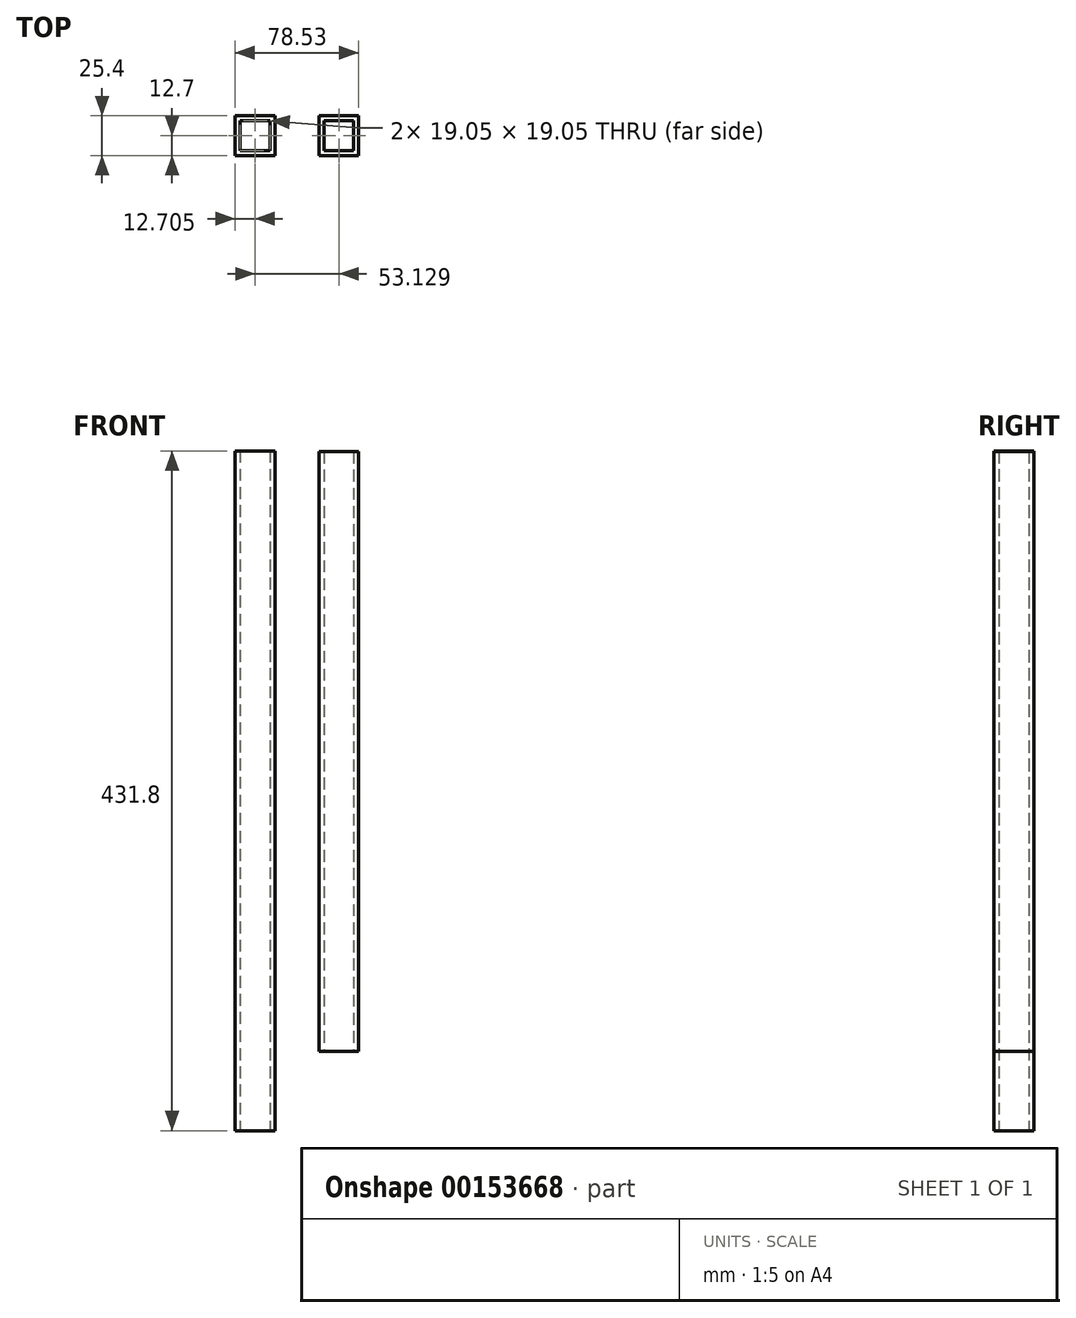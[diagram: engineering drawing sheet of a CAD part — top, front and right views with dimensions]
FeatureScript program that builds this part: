
annotation { "Feature Type Name" : "Feature", "Feature Type Description" : "" }
export const myFeature = defineFeature(function(context is Context, id is Id, definition is map)
    precondition{}
    {
        {
            var Q0;
            Q0=qCreatedBy(makeId("Front.planeOp"),FACE);
            var sketch = newSketch(context, id + "F0", { "sketchPlane" : qUnion([Q0])});
            skLineSegment(sketch, "E0.bottom", {"start": v(-31.27, 411.59) * mm, "end": v(-5.87, 411.59) * mm});
            skLineSegment(sketch, "E0.top", {"start": v(-31.27, -20.21) * mm, "end": v(-5.87, -20.21) * mm});
            skLineSegment(sketch, "E0.left", {"start": v(-31.27, 411.59) * mm, "end": v(-31.27, -20.21) * mm});
            skLineSegment(sketch, "E0.right", {"start": v(-5.87, 411.59) * mm, "end": v(-5.87, -20.21) * mm});
            skLineSegment(sketch, "E1.bottom", {"start": v(21.86, 411.06) * mm, "end": v(47.26, 411.06) * mm});
            skLineSegment(sketch, "E1.top", {"start": v(21.86, 30.06) * mm, "end": v(47.26, 30.06) * mm});
            skLineSegment(sketch, "E1.left", {"start": v(21.86, 411.06) * mm, "end": v(21.86, 30.06) * mm});
            skLineSegment(sketch, "E1.right", {"start": v(47.26, 411.06) * mm, "end": v(47.26, 30.06) * mm});
            skSolve(sketch);
        }
        {
            var Q0;
            Q0=qSketchRegion(id+"F0",true);
            extrude(context, id + "F1", {"entities" : qUnion([Q0]), "depth" : 25.4 * mm});
        }
        {
            var Q0;
            Q0=makeQuery(id+"F1.opExtrude","SWEPT_FACE",FACE,{"disambiguationData":[OSD([sQuery(id+"F0.wireOp",EDGE,"E0.bottom")])]});
            var Q1;
            Q1=makeQuery(id+"F1.opExtrude","SWEPT_FACE",FACE,{"disambiguationData":[OSD([sQuery(id+"F0.wireOp",EDGE,"E1.bottom")])]});
            var Q2;
            Q2=makeQuery(id+"F1.opExtrude","SWEPT_FACE",FACE,{"disambiguationData":[OSD([sQuery(id+"F0.wireOp",EDGE,"E1.top")])]});
            var Q3;
            Q3=makeQuery(id+"F1.opExtrude","SWEPT_FACE",FACE,{"disambiguationData":[OSD([sQuery(id+"F0.wireOp",EDGE,"E0.top")])]});
            shell(context, id + "F2", {"entities" : qUnion([Q0, Q1, Q2, Q3]), "thickness" : 3.17 * mm});
        }
    });
